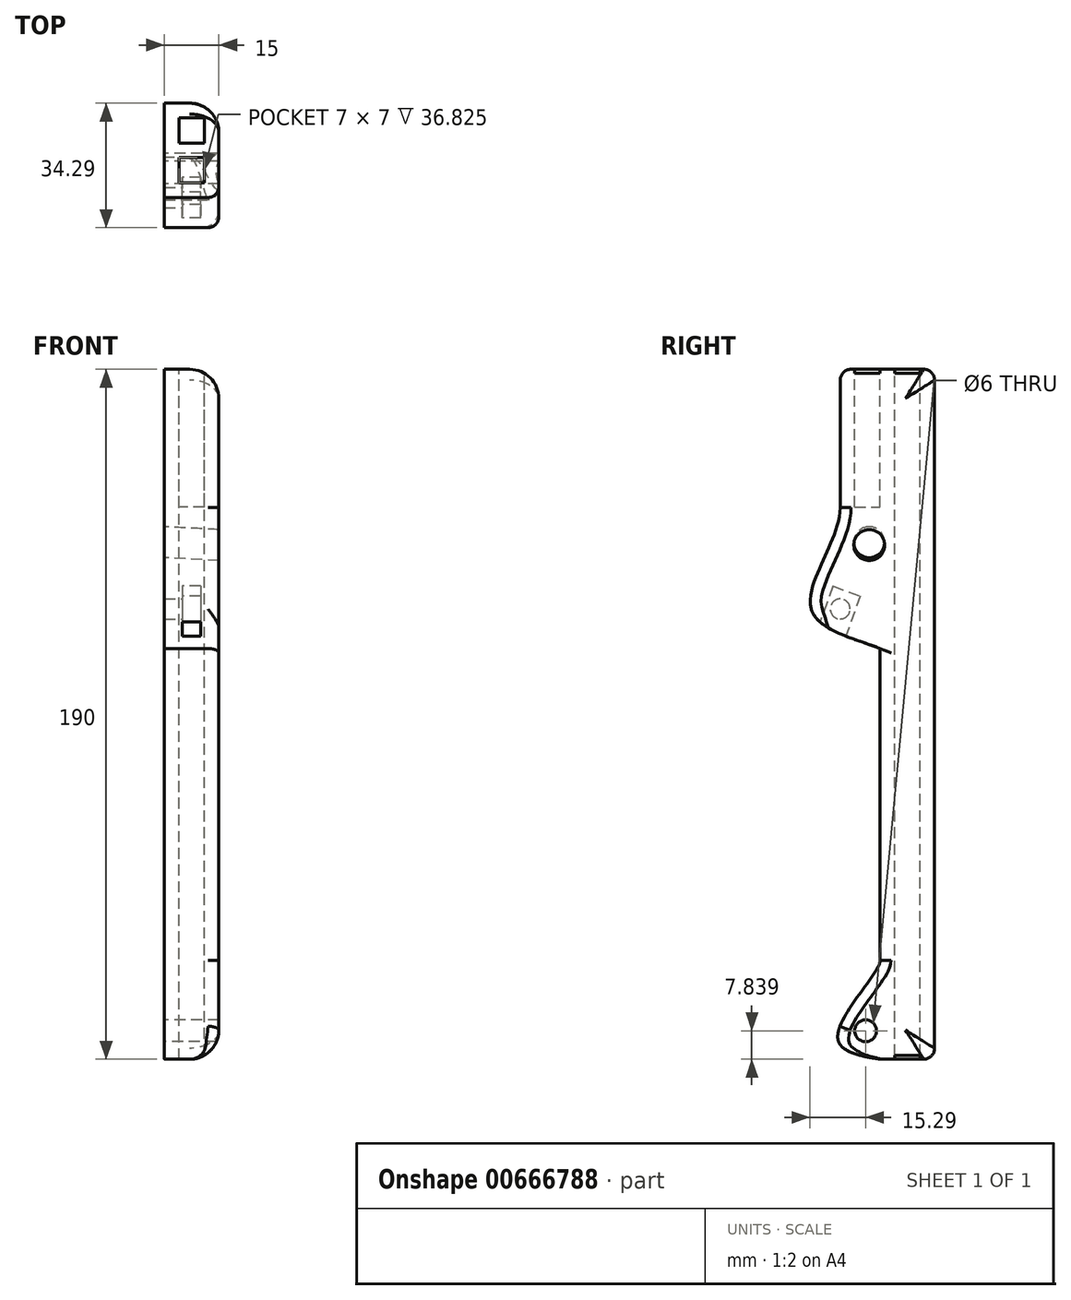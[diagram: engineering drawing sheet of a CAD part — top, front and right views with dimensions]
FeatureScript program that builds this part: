
annotation { "Feature Type Name" : "Feature", "Feature Type Description" : "" }
export const myFeature = defineFeature(function(context is Context, id is Id, definition is map)
    precondition{}
    {
        {
            var Q0;
            Q0=qCreatedBy(makeId("Right.planeOp"),FACE);
            var sketch = newSketch(context, id + "F0", { "sketchPlane" : qUnion([Q0])});
            skLineSegment(sketch, "E0.bottom", {"start": v(7.5, -95) * mm, "end": v(-7.5, -95) * mm});
            skLineSegment(sketch, "E0.top", {"start": v(7.5, 95) * mm, "end": v(-7.5, 95) * mm});
            skLineSegment(sketch, "E0.left", {"start": v(7.5, -95) * mm, "end": v(7.5, 95) * mm});
            skLineSegment(sketch, "E0.right", {"start": v(-7.5, -95) * mm, "end": v(-7.5, 95) * mm});
            skPoint(sketch, "E0.middle", {"position": v(0, 0) * mm});
            skSolve(sketch);
        }
        {
            var Q0;
            Q0 = qSketchRegion(id + "F0", true);
            extrude(context, id + "F1", {"entities" : qUnion([Q0]), "endBound" : BoundingType.SYMMETRIC, "depth" : 15 * mm, "offsetDistance" : 25 * mm});
        }
        {
            var Q0;
            Q0=makeQuery(id+"F1.opExtrude","SWEPT_FACE",FACE,{"disambiguationData":[OSD([sQuery(id+"F0.wireOp",EDGE,"E0.top")])]});
            var sketch = newSketch(context, id + "F2", { "sketchPlane" : qUnion([Q0])});
            skLineSegment(sketch, "E1.bottom", {"start": v(3.5, 3.5) * mm, "end": v(-3.5, 3.5) * mm});
            skLineSegment(sketch, "E1.top", {"start": v(3.5, -3.5) * mm, "end": v(-3.5, -3.5) * mm});
            skLineSegment(sketch, "E1.left", {"start": v(3.5, 3.5) * mm, "end": v(3.5, -3.5) * mm});
            skLineSegment(sketch, "E1.right", {"start": v(-3.5, 3.5) * mm, "end": v(-3.5, -3.5) * mm});
            skPoint(sketch, "E1.middle", {"position": v(0, 0) * mm});
            skSolve(sketch);
        }
        {
            var Q0;
            Q0 = qSketchRegion(id + "F2", true);
            extrude(context, id + "F3", {"entities" : qUnion([Q0]), "operationType" : NewBodyOperationType.REMOVE, "endBound" : BoundingType.THROUGH_ALL, "oppositeDirection" : true, "depth" : 25 * mm, "offsetDistance" : 25 * mm});
        }
        {
            var Q0;
            Q0=makeQuery(id+"F1.opExtrude","CAP_FACE",FACE,{"disambiguationData":[OSD([sQuery(id+"F0.wireOp",EDGE,"E0.bottom"),sQuery(id+"F0.wireOp",EDGE,"E0.top"),sQuery(id+"F0.wireOp",EDGE,"E0.left"),sQuery(id+"F0.wireOp",EDGE,"E0.right")])],"isStart":false});
            var sketch = newSketch(context, id + "F4", { "sketchPlane" : qUnion([Q0])});
            skLineSegment(sketch, "E2", {"start": v(-7.5, 95) * mm, "end": v(-18.5, 95) * mm});
            skLineSegment(sketch, "E3", {"start": v(-18.5, 95) * mm, "end": v(-18.5, 50) * mm});
            skLineSegment(sketch, "E4", {"start": v(-18.5, 50) * mm, "end": v(-7.5, 50) * mm});
            skSolve(sketch);
        }
        {
            var Q0;
            {var subQ0=sQuery(id+"F4.wireOp",EDGE,"E2");Q0=makeQuery(id+"F4.imprint","IMPRINT",FACE,{"disambiguationData":[TD([[makeQuery(id+"F4.imprint","IMPRINT",EDGE,{"derivedFrom":subQ0}),1.0]])]});}
            extrude(context, id + "F5", {"entities" : qUnion([Q0]), "operationType" : NewBodyOperationType.ADD, "oppositeDirection" : true, "depth" : 15 * mm, "offsetDistance" : 25 * mm});
        }
        {
            var Q0;
            Q0=makeQuery(id+"F5.boolean.opBoolean","MERGE",FACE,{"derivedFrom":[makeQuery(id+"F1.opExtrude","SWEPT_FACE",FACE,{"disambiguationData":[OSD([sQuery(id+"F0.wireOp",EDGE,"E0.top")])]}),makeQuery(id+"F5.opExtrude","SWEPT_FACE",FACE,{"disambiguationData":[OSD([sQuery(id+"F4.wireOp",EDGE,"E2")])]})]});
            var sketch = newSketch(context, id + "F6", { "sketchPlane" : qUnion([Q0])});
            skLineSegment(sketch, "E5", {"start": v(-3.5, -7.5) * mm, "end": v(3.5, -7.5) * mm});
            skLineSegment(sketch, "E6", {"start": v(3.5, -7.5) * mm, "end": v(3.5, -14.5) * mm});
            skLineSegment(sketch, "E7", {"start": v(3.5, -14.5) * mm, "end": v(-3.5, -14.5) * mm});
            skLineSegment(sketch, "E8", {"start": v(-3.5, -14.5) * mm, "end": v(-3.5, -7.5) * mm});
            skSolve(sketch);
        }
        {
            var Q0;
            Q0=makeQuery(id+"F6.imprint","IMPRINT",FACE,{"disambiguationData":[TD([[makeQuery(id+"F6.imprint","IMPRINT",EDGE,{"derivedFrom":sQuery(id+"F6.wireOp",EDGE,"E5")}),-1.0]])]});
            extrude(context, id + "F7", {"entities" : qUnion([Q0]), "operationType" : NewBodyOperationType.REMOVE, "oppositeDirection" : true, "depth" : 40 * mm, "offsetDistance" : 25 * mm});
        }
        {
            var Q0;
            Q0=qCreatedBy(makeId("Right.planeOp"),FACE);
            var sketch = newSketch(context, id + "F8", { "sketchPlane" : qUnion([Q0])});
            skPoint(sketch, "E9", {"position": v(-10.5, 47) * mm});
            skSolve(sketch);
        }
        {
            var Q0;
            Q0=qCreatedBy(makeId("Right.planeOp"),FACE);
            var sketch = newSketch(context, id + "F9", { "sketchPlane" : qUnion([Q0])});
            skPoint(sketch, "E10", {"position": v(-18.5, 29) * mm});
            skPoint(sketch, "E11", {"position": v(-7.5, 18.1) * mm});
            skLineSegment(sketch, "E12", {"start": v(-18.5, 29) * mm, "end": v(-26.5, 29) * mm});
            skFitSpline(sketch, "E13", {"points": [v(-18.5, 57.1) * mm, v(-26.5, 29) * mm, v(-7.5, 18.1) * mm], "startDerivative": vector(0.32, -51.24) * mm, "endDerivative": vector(40, -16.22) * mm});
            skLineSegment(sketch, "E14", {"start": v(-18.5, 57.1) * mm, "end": v(-7.5, 57.1) * mm});
            skLineSegment(sketch, "E15", {"start": v(-7.5, 18.1) * mm, "end": v(-7.5, 57.1) * mm});
            skSolve(sketch);
        }
        {
            var Q0;
            Q0 = qSketchRegion(id + "F9", true);
            extrude(context, id + "F10", {"entities" : qUnion([Q0]), "endBound" : BoundingType.SYMMETRIC, "depth" : 15 * mm, "offsetDistance" : 25 * mm});
        }
        {
            var Q0;
            Q0=makeQuery(id+"F10.opExtrude","SWEPT_BODY",BODY,{"disambiguationData":[OSD([sQuery(id+"F9.wireOp",EDGE,"E13"),sQuery(id+"F9.wireOp",EDGE,"E14"),sQuery(id+"F9.wireOp",EDGE,"E15")])]});
            var Q1;
            Q1=makeQuery(id+"F1.opExtrude","SWEPT_BODY",BODY,{"disambiguationData":[OSD([sQuery(id+"F0.wireOp",EDGE,"E0.bottom"),sQuery(id+"F0.wireOp",EDGE,"E0.top"),sQuery(id+"F0.wireOp",EDGE,"E0.left"),sQuery(id+"F0.wireOp",EDGE,"E0.right")])]});
            booleanBodies(context, id + "F11", {"operationType" : BooleanOperationType.UNION, "tools" : qUnion([Q0, Q1])});
        }
        {
            var Q0;
            Q0=sQuery(id+"F9.wireOp",VERTEX,"E10");
            var Q1;
            Q1=makeQuery(id+"F10.opExtrude","SWEPT_BODY",BODY,{"disambiguationData":[OSD([sQuery(id+"F9.wireOp",EDGE,"E13"),sQuery(id+"F9.wireOp",EDGE,"E14"),sQuery(id+"F9.wireOp",EDGE,"E15")])]});
            hole(context, id + "F12", {"style" : HoleStyle.SIMPLE, "endStyle" : HoleEndStyle.BLIND, "standardTappedOrClearance" : lookupTablePath({ "standard" : "ISO", "fit" : "Normal", "size" : "M5", "type" : "Clearance" }), "standardBlindInLast" : lookupTablePath({ "fit" : "Standard", "standard" : "ISO", "size" : "M5", "type" : "Clearance" }), "holeDiameter" : 5.5 * mm, "majorDiameter" : 5 * mm, "holeDepth" : 12 * mm, "isTappedThrough" : true, "tappedDepth" : 12 * mm, "tapClearance" : 3, "locations" : qUnion([Q0]), "scope" : qUnion([Q1])});
        }
        {
            var Q0;
            Q0=qCreatedBy(makeId("Front.planeOp"),FACE);
            var Q1;
            Q1=makeQuery(id+"F1.opExtrude","SWEPT_EDGE",EDGE,{"disambiguationData":[OSD([sQuery(id+"F0.wireOp",EDGE,"E0.bottom"),sQuery(id+"F0.wireOp",EDGE,"E0.right")])]});
            cPlane(context, id + "F13", {"entities" : qUnion([Q0, Q1]), "cplaneType" : CPlaneType.LINE_ANGLE, "offset" : 40 * mm, "angle" : 70 * degree, "oppositeDirection" : true, "width" : 150 * mm, "height" : 150 * mm});
        }
        {
            var Q0;
            Q0=qCreatedBy(makeId("Right.planeOp"),FACE);
            var Q1;
            Q1=makeQuery(id+"F5.boolean.opBoolean","MERGE",EDGE,{"derivedFrom":[makeQuery(id+"F1.opExtrude","CAP_EDGE",EDGE,{"disambiguationData":[OSD([sQuery(id+"F0.wireOp",EDGE,"E0.top")])],"isStart":false}),makeQuery(id+"F5.opExtrude","CAP_EDGE",EDGE,{"disambiguationData":[OSD([sQuery(id+"F4.wireOp",EDGE,"E2")])],"isStart":true})]});
            cPlane(context, id + "F14", {"entities" : qUnion([Q0, Q1]), "cplaneType" : CPlaneType.LINE_ANGLE, "offset" : 25 * mm, "angle" : 3 * degree, "oppositeDirection" : true, "width" : 150 * mm, "height" : 150 * mm});
        }
        {
            var Q0;
            Q0=qCreatedBy(id+"F14.planeOp",FACE);
            var sketch = newSketch(context, id + "F15", { "sketchPlane" : qUnion([Q0])});
            skCircle(sketch, "E16", {"center": v(10.5, 46.94) * mm, "radius": 4.25 * mm});
            skSolve(sketch);
        }
        {
            var Q0;
            Q0 = qSketchRegion(id + "F15", true);
            extrude(context, id + "F16", {"entities" : qUnion([Q0]), "operationType" : NewBodyOperationType.REMOVE, "endBound" : BoundingType.SYMMETRIC, "oppositeDirection" : true, "depth" : 50 * mm, "offsetDistance" : 25 * mm});
        }
        {
            var Q0;
            Q0=qCreatedBy(makeId("Right.planeOp"),FACE);
            var sketch = newSketch(context, id + "F17", { "sketchPlane" : qUnion([Q0])});
            skPoint(sketch, "E17", {"position": v(-7.5, -95) * mm});
            skFitSpline(sketch, "E18", {"points": [v(-7.5, -95) * mm, v(-19.06, -89.77) * mm, v(-7.5, -67.81) * mm], "startDerivative": vector(-14.27, 3.2) * mm, "endDerivative": vector(-0.08, 18.34) * mm});
            skCircle(sketch, "E19", {"center": v(-11.5, -87.16) * mm, "radius": 3 * mm});
            skLineSegment(sketch, "E20", {"start": v(-7.5, -67.81) * mm, "end": v(-7.5, -95) * mm});
            skSolve(sketch);
        }
        {
            var Q0;
            Q0 = qSketchRegion(id + "F17", true);
            extrude(context, id + "F18", {"entities" : qUnion([Q0]), "operationType" : NewBodyOperationType.ADD, "endBound" : BoundingType.SYMMETRIC, "depth" : 15 * mm, "offsetDistance" : 25 * mm});
        }
        {
            var Q0;
            Q0=qCreatedBy(id+"F13.planeOp",FACE);
            var sketch = newSketch(context, id + "F19", { "sketchPlane" : qUnion([Q0])});
            skLineSegment(sketch, "E21.bottom", {"start": v(2.5, -31.3) * mm, "end": v(-2.5, -31.3) * mm});
            skLineSegment(sketch, "E21.top", {"start": v(2.5, -23.3) * mm, "end": v(-2.5, -23.3) * mm});
            skLineSegment(sketch, "E21.left", {"start": v(2.5, -31.3) * mm, "end": v(2.5, -23.3) * mm});
            skLineSegment(sketch, "E21.right", {"start": v(-2.5, -31.3) * mm, "end": v(-2.5, -23.3) * mm});
            skPoint(sketch, "E21.middle", {"position": v(0, -27.3) * mm});
            skSolve(sketch);
        }
        {
            var Q0;
            Q0=makeQuery(id+"F19.imprint","IMPRINT",FACE,{"disambiguationData":[TD([[makeQuery(id+"F19.imprint","IMPRINT",EDGE,{"derivedFrom":sQuery(id+"F19.wireOp",EDGE,"E21.bottom")}),-1.0]])]});
            extrude(context, id + "F20", {"entities" : qUnion([Q0]), "operationType" : NewBodyOperationType.REMOVE, "depth" : 118 * mm, "offsetDistance" : 25 * mm});
        }
        {
            var Q0;
            Q0=makeQuery(id+"F1.opExtrude","CAP_EDGE",EDGE,{"disambiguationData":[OSD([sQuery(id+"F0.wireOp",EDGE,"E0.left")])],"isStart":false});
            var Q1;
            Q1=makeQuery(id+"F5.boolean.opBoolean","MERGE",EDGE,{"derivedFrom":[makeQuery(id+"F1.opExtrude","CAP_EDGE",EDGE,{"disambiguationData":[OSD([sQuery(id+"F0.wireOp",EDGE,"E0.top")])],"isStart":false}),makeQuery(id+"F5.opExtrude","CAP_EDGE",EDGE,{"disambiguationData":[OSD([sQuery(id+"F4.wireOp",EDGE,"E2")])],"isStart":true})]});
            var Q2;
            Q2=makeQuery(id+"F1.opExtrude","CAP_EDGE",EDGE,{"disambiguationData":[OSD([sQuery(id+"F0.wireOp",EDGE,"E0.bottom")])],"isStart":false});
            fillet(context, id + "F21", {"entities" : qUnion([Q0, Q1, Q2]), "radius" : 8 * mm, "tangentPropagation" : true, "allowEdgeOverflow" : false});
        }
        {
            var Q0;
            Q0=makeQuery(id+"F5.opExtrude","CAP_EDGE",EDGE,{"disambiguationData":[OSD([sQuery(id+"F4.wireOp",EDGE,"E3")])],"isStart":true});
            var Q1;
            Q1=makeQuery(id+"F1.opExtrude","CAP_EDGE",EDGE,{"disambiguationData":[OSD([sQuery(id+"F0.wireOp",EDGE,"E0.right")])],"isStart":false});
            var Q2;
            Q2=makeQuery(id+"F18.opExtrude","CAP_EDGE",EDGE,{"disambiguationData":[OSD([sQuery(id+"F17.wireOp",EDGE,"E18")])],"isStart":false});
            var Q3;
            Q3=makeQuery(id+"F21.opFillet","BLEND_EDGE",EDGE,{"blendedFrom":[makeQuery(id+"F1.opExtrude","CAP_EDGE",EDGE,{"disambiguationData":[OSD([sQuery(id+"F0.wireOp",EDGE,"E0.bottom")])],"isStart":false}),makeQuery(id+"F1.opExtrude","CAP_EDGE",EDGE,{"disambiguationData":[OSD([sQuery(id+"F0.wireOp",EDGE,"E0.left")])],"isStart":false})],"blendedInto":[]});
            var Q4;
            Q4=makeQuery(id+"F21.opFillet","BLEND_EDGE",EDGE,{"blendedFrom":[makeQuery(id+"F1.opExtrude","CAP_EDGE",EDGE,{"disambiguationData":[OSD([sQuery(id+"F0.wireOp",EDGE,"E0.left")])],"isStart":false}),makeQuery(id+"F5.boolean.opBoolean","MERGE",EDGE,{"derivedFrom":[makeQuery(id+"F1.opExtrude","CAP_EDGE",EDGE,{"disambiguationData":[OSD([sQuery(id+"F0.wireOp",EDGE,"E0.top")])],"isStart":false}),makeQuery(id+"F5.opExtrude","CAP_EDGE",EDGE,{"disambiguationData":[OSD([sQuery(id+"F4.wireOp",EDGE,"E2")])],"isStart":true})]})],"blendedInto":[]});
            fillet(context, id + "F22", {"entities" : qUnion([Q0, Q1, Q2, Q3, Q4]), "radius" : 3 * mm, "tangentPropagation" : true, "allowEdgeOverflow" : false});
        }
    });
